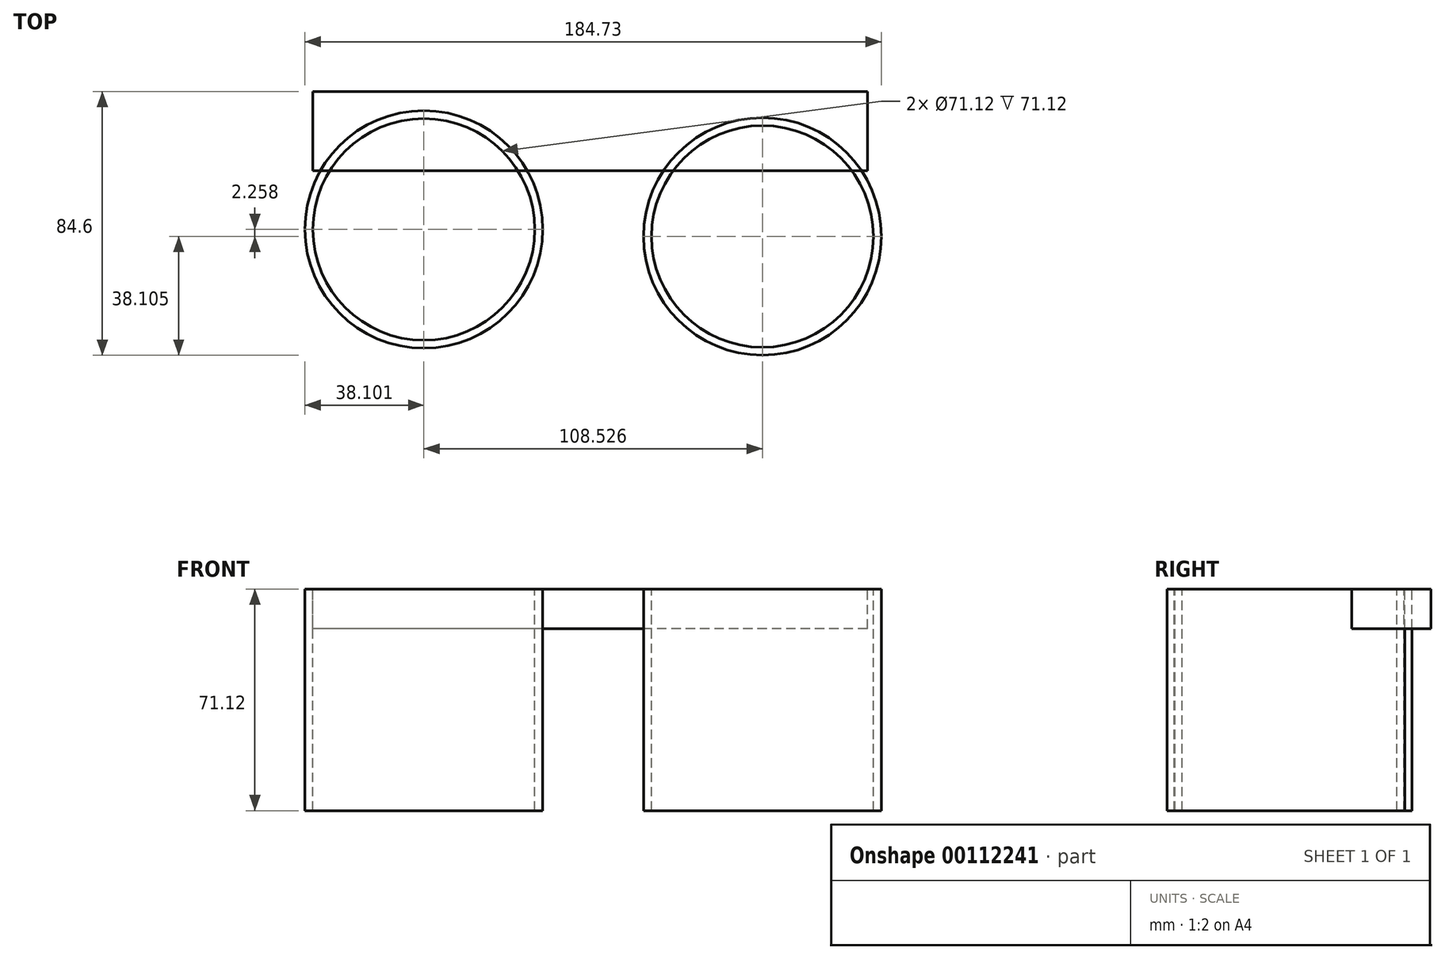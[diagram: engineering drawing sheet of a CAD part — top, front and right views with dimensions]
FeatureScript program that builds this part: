
annotation { "Feature Type Name" : "Feature", "Feature Type Description" : "" }
export const myFeature = defineFeature(function(context is Context, id is Id, definition is map)
    precondition{}
    {
        {
            var Q0;
            Q0=qCreatedBy(makeId("Front.planeOp"),FACE);
            var sketch = newSketch(context, id + "F0", { "sketchPlane" : qUnion([Q0])});
            skLineSegment(sketch, "E0.bottom", {"start": v(88.9, -6.35) * mm, "end": v(-88.9, -6.35) * mm});
            skLineSegment(sketch, "E0.top", {"start": v(88.9, 6.35) * mm, "end": v(-88.9, 6.35) * mm});
            skLineSegment(sketch, "E0.left", {"start": v(88.9, -6.35) * mm, "end": v(88.9, 6.35) * mm});
            skLineSegment(sketch, "E0.right", {"start": v(-88.9, -6.35) * mm, "end": v(-88.9, 6.35) * mm});
            skPoint(sketch, "E0.middle", {"position": v(0, 0) * mm});
            skSolve(sketch);
        }
        {
            var Q0;
            Q0 = qSketchRegion(id + "F0", true);
            extrude(context, id + "F1", {"entities" : qUnion([Q0]), "depth" : 25.4 * mm});
        }
        {
            var Q0;
            Q0=makeQuery(id+"F1.opExtrude","SWEPT_FACE",FACE,{"disambiguationData":[OSD([sQuery(id+"F0.wireOp",EDGE,"E0.top")])]});
            var sketch = newSketch(context, id + "F2", { "sketchPlane" : qUnion([Q0])});
            skCircle(sketch, "E1", {"center": v(-53.25, -44.24) * mm, "radius": 38.1 * mm});
            skCircle(sketch, "E2", {"center": v(55.28, -46.5) * mm, "radius": 38.1 * mm});
            skCircle(sketch, "E3", {"center": v(-53.25, -44.24) * mm, "radius": 35.56 * mm});
            skCircle(sketch, "E4", {"center": v(55.28, -46.5) * mm, "radius": 35.56 * mm});
            skSolve(sketch);
        }
        {
            var Q0;
            Q0 = qSketchRegion(id + "F2", true);
            extrude(context, id + "F3", {"entities" : qUnion([Q0]), "oppositeDirection" : true, "depth" : 71.12 * mm});
        }
    });
